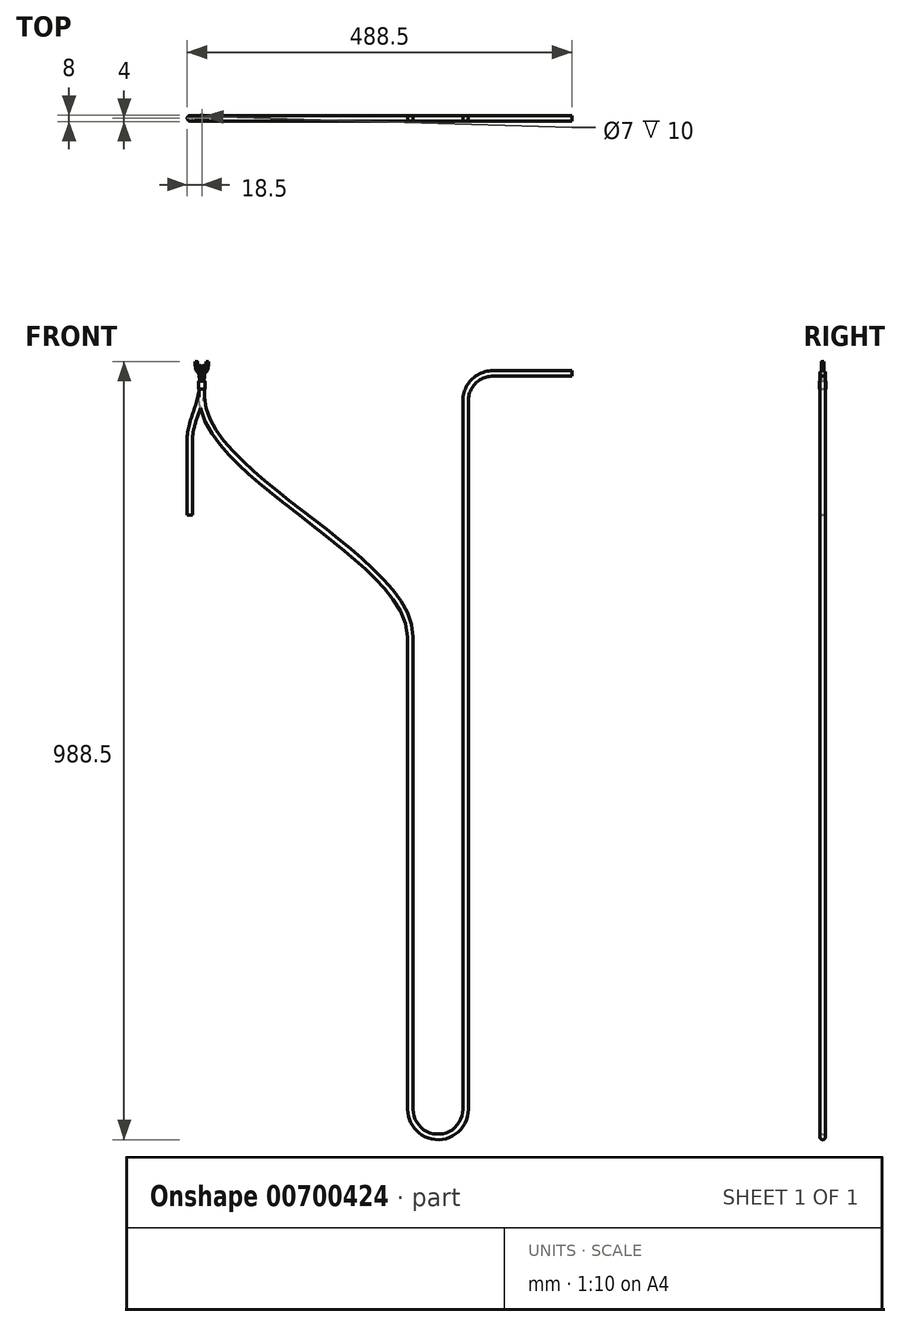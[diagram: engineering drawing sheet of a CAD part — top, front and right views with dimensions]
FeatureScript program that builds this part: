
annotation { "Feature Type Name" : "Feature", "Feature Type Description" : "" }
export const myFeature = defineFeature(function(context is Context, id is Id, definition is map)
    precondition{}
    {
        {
            var Q0;
            Q0=qCreatedBy(makeId("Top.planeOp"),FACE);
            var sketch = newSketch(context, id + "F0", { "sketchPlane" : qUnion([Q0])});
            skCircle(sketch, "E0", {"center": v(0, 0) * mm, "radius": 3.5 * mm});
            skSolve(sketch);
        }
        {
            var Q0;
            Q0=qCreatedBy(makeId("Front.planeOp"),FACE);
            var sketch = newSketch(context, id + "F1", { "sketchPlane" : qUnion([Q0])});
            skLineSegment(sketch, "E1", {"start": v(0, 0) * mm, "end": v(0, -10) * mm});
            skFitSpline(sketch, "E2", {"points": [v(0, -10) * mm, v(-15, -70) * mm], "startDerivative": vector(0, -45) * mm, "endDerivative": vector(0, -45) * mm});
            skLineSegment(sketch, "E3", {"start": v(-15, -70) * mm, "end": v(-15, -170) * mm});
            skSolve(sketch);
        }
        {
            var Q0;
            Q0=qSketchRegion(id+"F0",true);
            var Q1;
            Q1=qConstructionFilter(qBodyType(qCreatedBy(id+"F1",EDGE),BodyType.WIRE),ConstructionObject.NO);
            sweep(context, id + "F2", {"profiles" : qUnion([Q0]), "path" : qUnion([Q1])});
        }
        {
            var Q0;
            Q0=makeQuery(id+"F2.opSweep","CAP_FACE",FACE,{"disambiguationData":[OSD([sQuery(id+"F0.wireOp",EDGE,"E0"),sQuery(id+"F1.wireOp",VERTEX,"E1.start")])],"isStart":true});
            var sketch = newSketch(context, id + "F3", { "sketchPlane" : qUnion([Q0])});
            skCircle(sketch, "E4", {"center": v(1.5, 0) * mm, "radius": 1.5 * mm});
            skSolve(sketch);
        }
        {
            var Q0;
            Q0=qCreatedBy(makeId("Front.planeOp"),FACE);
            var sketch = newSketch(context, id + "F4", { "sketchPlane" : qUnion([Q0])});
            skFitSpline(sketch, "E5", {"points": [v(1.5, 0) * mm, v(2.5, 15) * mm], "startDerivative": vector(0, 15) * mm, "endDerivative": vector(0, 15) * mm});
            skLineSegment(sketch, "E6", {"start": v(2.5, 15) * mm, "end": v(2.5, 20) * mm});
            skSolve(sketch);
        }
        {
            var Q0;
            Q0=qSketchRegion(id+"F3",true);
            var Q1;
            Q1=qConstructionFilter(qBodyType(qCreatedBy(id+"F4",EDGE),BodyType.WIRE),ConstructionObject.NO);
            sweep(context, id + "F5", {"profiles" : qUnion([Q0]), "path" : qUnion([Q1])});
        }
        {
            var Q0;
            Q0=makeQuery(id+"F5.opSweep","SWEPT_BODY",BODY,{"disambiguationData":[OSD([sQuery(id+"F3.wireOp",EDGE,"E4"),sQuery(id+"F4.wireOp",EDGE,"E6")])]});
            var Q1;
            Q1=qCreatedBy(makeId("Right.planeOp"),FACE);
            mirror(context, id + "F6", {"entities" : qUnion([Q0]), "mirrorPlane" : qUnion([Q1])});
        }
        {
            var Q0;
            Q0=makeQuery(id+"F2.opSweep","CAP_FACE",FACE,{"disambiguationData":[OSD([sQuery(id+"F0.wireOp",EDGE,"E0"),sQuery(id+"F1.wireOp",VERTEX,"E1.start")])],"isStart":true});
            var sketch = newSketch(context, id + "F7", { "sketchPlane" : qUnion([Q0])});
            skCircle(sketch, "E7.0", {"center": v(0, 0) * mm, "radius": 3.5 * mm});
            skCircle(sketch, "E8.0", {"center": v(0, 0) * mm, "radius": 4 * mm});
            skSolve(sketch);
        }
        {
            var Q0;
            Q0=qSketchRegion(id+"F7",true);
            extrude(context, id + "F8", {"entities" : qUnion([Q0]), "oppositeDirection" : true, "depth" : 10 * mm, "offsetDistance" : 25 * mm});
        }
        {
            var Q0;
            Q0=qCreatedBy(makeId("Front.planeOp"),FACE);
            var sketch = newSketch(context, id + "F9", { "sketchPlane" : qUnion([Q0])});
            skFitSpline(sketch, "E9", {"points": [v(1.5, 0) * mm, v(4.25, 12.5) * mm, v(7, 25) * mm], "startDerivative": vector(0, 60) * mm, "endDerivative": vector(0, 60) * mm});
            skLineSegment(sketch, "E10", {"start": v(1.5, 10) * mm, "end": v(1.5, 0) * mm, "construction": true});
            skLineSegment(sketch, "E11", {"start": v(7, 25) * mm, "end": v(7, 15) * mm, "construction": true});
            skLineSegment(sketch, "E12", {"start": v(1.5, 0) * mm, "end": v(7, 25) * mm, "construction": true});
            skSolve(sketch);
        }
        {
            var Q0;
            Q0=qSketchRegion(id+"F3",true);
            var Q1;
            Q1=sQuery(id+"F9.wireOp",EDGE,"E9");
            sweep(context, id + "F10", {"profiles" : qUnion([Q0]), "path" : qUnion([Q1])});
        }
        {
            var Q0;
            Q0=makeQuery(id+"F10.opSweep","SWEPT_BODY",BODY,{"disambiguationData":[OSD([sQuery(id+"F3.wireOp",EDGE,"E4"),sQuery(id+"F9.wireOp",EDGE,"E9")])]});
            var Q1;
            Q1=qCreatedBy(makeId("Right.planeOp"),FACE);
            mirror(context, id + "F11", {"entities" : qUnion([Q0]), "mirrorPlane" : qUnion([Q1])});
        }
        {
            var Q0;
            Q0=qCreatedBy(makeId("Front.planeOp"),FACE);
            var sketch = newSketch(context, id + "F12", { "sketchPlane" : qUnion([Q0])});
            skLineSegment(sketch, "E13", {"start": v(265, -325) * mm, "end": v(265, -925) * mm});
            skArc(sketch, "E14", {"start": v(265, -925) * mm, "mid": v(300, -960) * mm, "end": v(335, -925) * mm});
            skLineSegment(sketch, "E15", {"start": v(335, -925) * mm, "end": v(335, -25) * mm});
            skArc(sketch, "E16", {"start": v(370, 10) * mm, "mid": v(345.25, -0.25) * mm, "end": v(335, -25) * mm});
            skLineSegment(sketch, "E17", {"start": v(370, 10) * mm, "end": v(470, 10) * mm});
            skFitSpline(sketch, "E18", {"points": [v(265, -325) * mm, v(132.5, -172.5) * mm, v(0, -20) * mm], "startDerivative": vector(0, 300) * mm, "endDerivative": vector(0, 300) * mm});
            skLineSegment(sketch, "E19", {"start": v(265, -275) * mm, "end": v(265, -325) * mm, "construction": true});
            skLineSegment(sketch, "E20", {"start": v(265, -325) * mm, "end": v(0, -20) * mm, "construction": true});
            skLineSegment(sketch, "E21", {"start": v(0, 0) * mm, "end": v(0, -20) * mm});
            skLineSegment(sketch, "E22", {"start": v(0, -70) * mm, "end": v(0, -20) * mm, "construction": true});
            skSolve(sketch);
        }
        {
            var Q0;
            Q0=qSketchRegion(id+"F0",true);
            var Q1;
            Q1=qConstructionFilter(qBodyType(qCreatedBy(id+"F12",EDGE),BodyType.WIRE),ConstructionObject.NO);
            sweep(context, id + "F13", {"profiles" : qUnion([Q0]), "path" : qUnion([Q1])});
        }
    });
